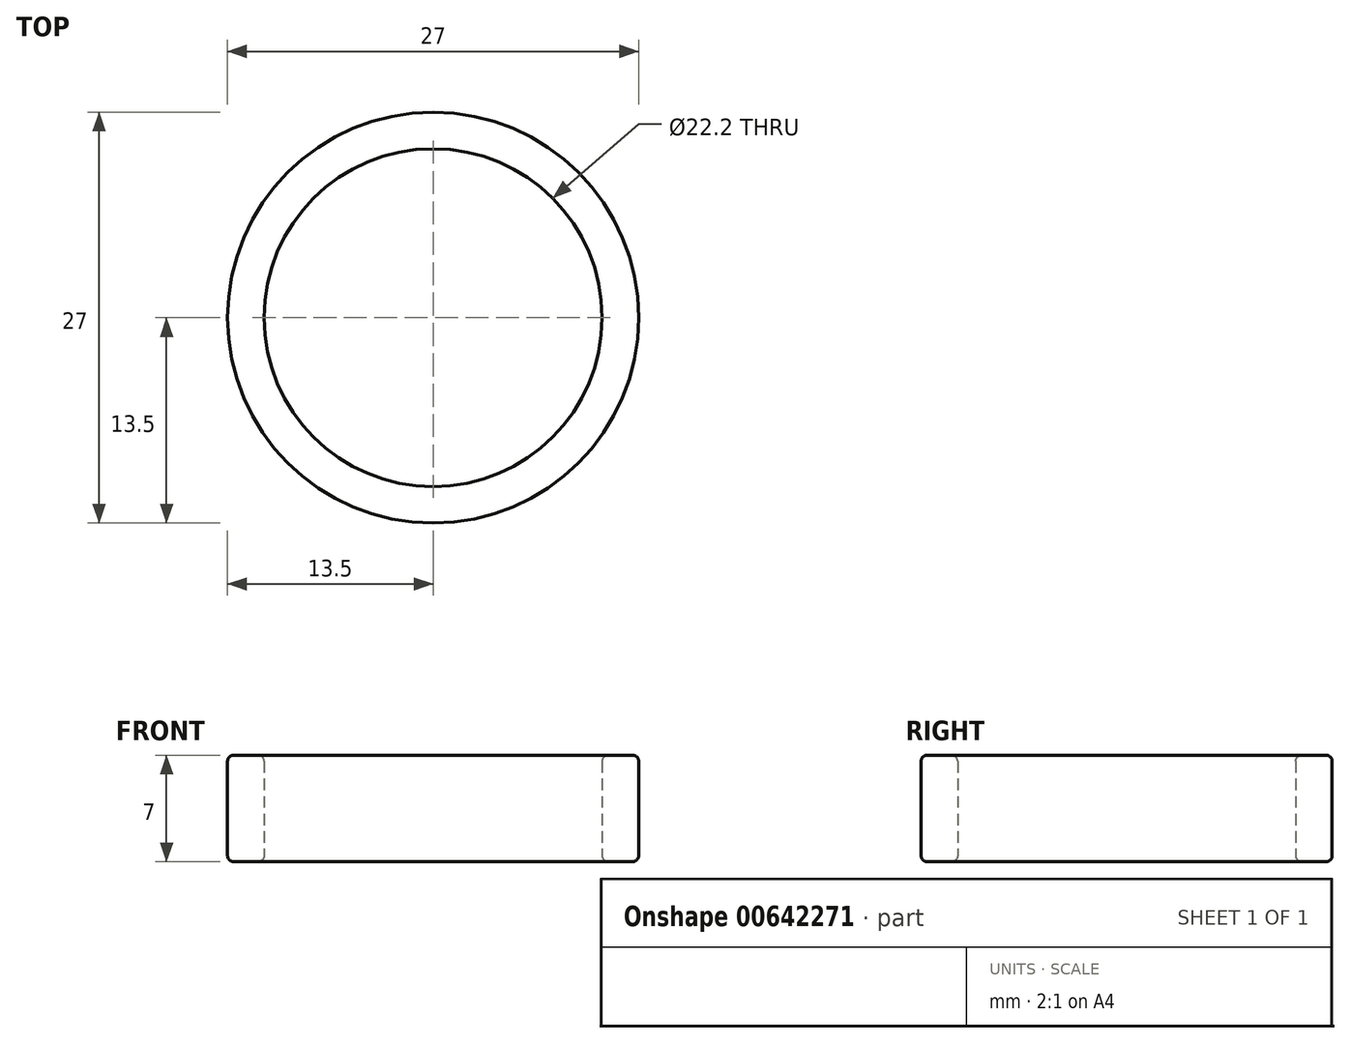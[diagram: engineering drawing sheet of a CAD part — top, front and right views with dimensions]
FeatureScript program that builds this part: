
annotation { "Feature Type Name" : "Feature", "Feature Type Description" : "" }
export const myFeature = defineFeature(function(context is Context, id is Id, definition is map)
    precondition{}
    {
        {
            var Q0;
            Q0=qCreatedBy(makeId("Top.planeOp"),FACE);
            var sketch = newSketch(context, id + "F0", { "sketchPlane" : qUnion([Q0])});
            skCircle(sketch, "E0", {"center": v(0, 0) * mm, "radius": 11.1 * mm});
            skCircle(sketch, "E1", {"center": v(0, 0) * mm, "radius": 13.5 * mm});
            skSolve(sketch);
        }
        {
            var Q0;
            Q0=makeQuery(id+"F0.imprint","IMPRINT",FACE,{"disambiguationData":[TD([[makeQuery(id+"F0.imprint","IMPRINT",EDGE,{"derivedFrom":sQuery(id+"F0.wireOp",EDGE,"E0")}),-1.0]])]});
            var Q1;
            {var subQ0=sQuery(id+"F0.wireOp",EDGE,"e56zxMKM-Kjhy-064L-GIG7-PTHqFccnnUyJ");var subQ1=sQuery(id+"F0.wireOp",EDGE,"E1");var subQ2=makeQuery(id+"F0.imprint","INTERSECT",VERTEX,{"derivedFrom":[subQ1,subQ0]});Q1=makeQuery(id+"F0.imprint","IMPRINT",FACE,{"disambiguationData":[TD([[makeQuery(id+"F0.imprint","IMPRINT",EDGE,{"disambiguationData":[TD([[subQ2,-1.0]])],"derivedFrom":subQ1}),-1.0]])]});}
            var Q2;
            Q2=makeQuery(id+"F0.imprint","IMPRINT",FACE,{"disambiguationData":[TD([[makeQuery(id+"F0.imprint","IMPRINT",EDGE,{"derivedFrom":sQuery(id+"F0.wireOp",EDGE,"0e4e4f05-918f-47c3-9332-bcd5f5d39093.1.4.0")}),-1.0]])]});
            var Q3;
            {var subQ0=sQuery(id+"F0.wireOp",EDGE,"2f779958-1fc4-4bb9-a079-996d55da559e.1.0");var subQ1=sQuery(id+"F0.wireOp",EDGE,"E1");var subQ2=makeQuery(id+"F0.imprint","INTERSECT",VERTEX,{"derivedFrom":[subQ1,subQ0]});Q3=makeQuery(id+"F0.imprint","IMPRINT",FACE,{"disambiguationData":[TD([[makeQuery(id+"F0.imprint","IMPRINT",EDGE,{"disambiguationData":[TD([[subQ2,-1.0]])],"derivedFrom":subQ1}),-1.0]])]});}
            var Q4;
            Q4=makeQuery(id+"F0.imprint","IMPRINT",FACE,{"disambiguationData":[TD([[makeQuery(id+"F0.imprint","IMPRINT",EDGE,{"derivedFrom":sQuery(id+"F0.wireOp",EDGE,"hkNb2Qpd-5HZF-mSI6-sH4i-8EYBwDvRSwwR")}),-1.0]])]});
            var Q5;
            {var subQ0=sQuery(id+"F0.wireOp",EDGE,"2f779958-1fc4-4bb9-a079-996d55da559e.2.0");var subQ1=sQuery(id+"F0.wireOp",EDGE,"E1");var subQ2=makeQuery(id+"F0.imprint","INTERSECT",VERTEX,{"derivedFrom":[subQ1,subQ0]});Q5=makeQuery(id+"F0.imprint","IMPRINT",FACE,{"disambiguationData":[TD([[makeQuery(id+"F0.imprint","IMPRINT",EDGE,{"disambiguationData":[TD([[subQ2,-1.0]])],"derivedFrom":subQ1}),-1.0]])]});}
            var Q6;
            Q6=makeQuery(id+"F0.imprint","IMPRINT",FACE,{"disambiguationData":[TD([[makeQuery(id+"F0.imprint","IMPRINT",EDGE,{"derivedFrom":sQuery(id+"F0.wireOp",EDGE,"2dce2605-6ec3-4248-8eab-4bc886ecd383.1.0")}),-1.0]])]});
            var Q7;
            {var subQ0=sQuery(id+"F0.wireOp",EDGE,"2f779958-1fc4-4bb9-a079-996d55da559e.3.0");var subQ1=sQuery(id+"F0.wireOp",EDGE,"E1");var subQ2=makeQuery(id+"F0.imprint","INTERSECT",VERTEX,{"derivedFrom":[subQ1,subQ0]});Q7=makeQuery(id+"F0.imprint","IMPRINT",FACE,{"disambiguationData":[TD([[makeQuery(id+"F0.imprint","IMPRINT",EDGE,{"disambiguationData":[TD([[subQ2,-1.0]])],"derivedFrom":subQ1}),-1.0]])]});}
            var Q8;
            Q8=makeQuery(id+"F0.imprint","IMPRINT",FACE,{"disambiguationData":[TD([[makeQuery(id+"F0.imprint","IMPRINT",EDGE,{"derivedFrom":sQuery(id+"F0.wireOp",EDGE,"2dce2605-6ec3-4248-8eab-4bc886ecd383.2.0")}),-1.0]])]});
            var Q9;
            {var subQ0=sQuery(id+"F0.wireOp",EDGE,"2f779958-1fc4-4bb9-a079-996d55da559e.4.0");var subQ1=sQuery(id+"F0.wireOp",EDGE,"E1");var subQ2=makeQuery(id+"F0.imprint","INTERSECT",VERTEX,{"derivedFrom":[subQ1,subQ0]});Q9=makeQuery(id+"F0.imprint","IMPRINT",FACE,{"disambiguationData":[TD([[makeQuery(id+"F0.imprint","IMPRINT",EDGE,{"disambiguationData":[TD([[subQ2,-1.0]])],"derivedFrom":subQ1}),-1.0]])]});}
            var Q10;
            Q10=makeQuery(id+"F0.imprint","IMPRINT",FACE,{"disambiguationData":[TD([[makeQuery(id+"F0.imprint","IMPRINT",EDGE,{"derivedFrom":sQuery(id+"F0.wireOp",EDGE,"0e4e4f05-918f-47c3-9332-bcd5f5d39093.1.3.0")}),-1.0]])]});
            extrude(context, id + "F1", {"entities" : qUnion([Q0, Q1, Q2, Q3, Q4, Q5, Q6, Q7, Q8, Q9, Q10]), "depth" : 7 * mm, "offsetDistance" : 25 * mm});
        }
        {
            var Q0;
            Q0=makeQuery(id+"F1.opExtrude","CAP_EDGE",EDGE,{"disambiguationData":[OSD([sQuery(id+"F0.wireOp",EDGE,"E0")])],"isStart":false});
            var Q1;
            Q1=makeQuery(id+"F1.opExtrude","CAP_EDGE",EDGE,{"disambiguationData":[OSD([sQuery(id+"F0.wireOp",EDGE,"E1")])],"isStart":false});
            var Q2;
            Q2=makeQuery(id+"F1.opExtrude","CAP_FACE",FACE,{"disambiguationData":[OSD([sQuery(id+"F0.wireOp",EDGE,"E0"),sQuery(id+"F0.wireOp",EDGE,"E1")])],"isStart":true});
            fillet(context, id + "F2", {"entities" : qUnion([Q0, Q1, Q2]), "radius" : .4 * mm, "tangentPropagation" : true, "allowEdgeOverflow" : false});
        }
    });
